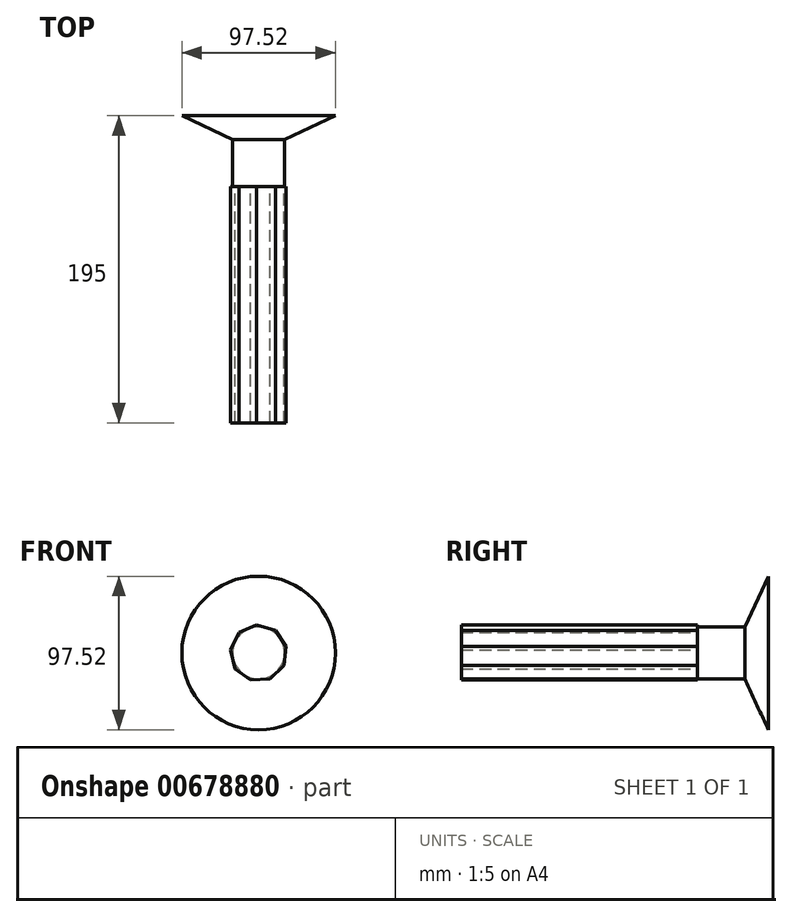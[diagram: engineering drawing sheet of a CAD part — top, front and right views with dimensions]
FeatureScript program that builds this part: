
annotation { "Feature Type Name" : "Feature", "Feature Type Description" : "" }
export const myFeature = defineFeature(function(context is Context, id is Id, definition is map)
    precondition{}
    {
        {
            var Q0;
            Q0=qCreatedBy(makeId("Front.planeOp"),FACE);
            var sketch = newSketch(context, id + "F0", { "sketchPlane" : qUnion([Q0])});
            skLineSegment(sketch, "E0.0", {"start": v(7.22, -16.4) * mm, "end": v(-5.01, -17.2) * mm});
            skLineSegment(sketch, "E0.1", {"start": v(-5.01, -17.2) * mm, "end": v(-14.9, -9.95) * mm});
            skLineSegment(sketch, "E0.2", {"start": v(-14.9, -9.95) * mm, "end": v(-17.8, 1.95) * mm});
            skLineSegment(sketch, "E0.3", {"start": v(-17.8, 1.95) * mm, "end": v(-12.39, 12.94) * mm});
            skLineSegment(sketch, "E0.4", {"start": v(-12.39, 12.94) * mm, "end": v(-1.17, 17.88) * mm});
            skLineSegment(sketch, "E0.5", {"start": v(-1.17, 17.88) * mm, "end": v(10.6, 14.45) * mm});
            skLineSegment(sketch, "E0.6", {"start": v(10.6, 14.45) * mm, "end": v(17.4, 4.26) * mm});
            skLineSegment(sketch, "E0.7", {"start": v(17.4, 4.26) * mm, "end": v(16.07, -7.92) * mm});
            skLineSegment(sketch, "E0.8", {"start": v(16.07, -7.92) * mm, "end": v(7.22, -16.4) * mm});
            skSolve(sketch);
        }
        {
            var Q0;
            Q0=makeQuery(id+"F0.imprint","IMPRINT",FACE,{"disambiguationData":[TD([[makeQuery(id+"F0.imprint","IMPRINT",EDGE,{"derivedFrom":sQuery(id+"F0.wireOp",EDGE,"E0.0")}),-1.0]])]});
            extrude(context, id + "F1", {"entities" : qUnion([Q0]), "depth" : 150 * mm, "offsetDistance" : 25 * mm});
        }
        {
            var Q0;
            Q0=qCreatedBy(makeId("Front.planeOp"),FACE);
            var sketch = newSketch(context, id + "F2", { "sketchPlane" : qUnion([Q0])});
            skCircle(sketch, "E1", {"center": v(0, 0) * mm, "radius": 16.6 * mm});
            skSolve(sketch);
        }
        {
            var Q0;
            Q0=makeQuery(id+"F2.imprint","IMPRINT",FACE,{"disambiguationData":[TD([[makeQuery(id+"F2.imprint","IMPRINT",EDGE,{"derivedFrom":sQuery(id+"F2.wireOp",EDGE,"E1")}),1.0]])]});
            extrude(context, id + "F3", {"entities" : qUnion([Q0]), "operationType" : NewBodyOperationType.ADD, "oppositeDirection" : true, "depth" : 30 * mm, "offsetDistance" : 25 * mm});
        }
        {
            var Q0;
            Q0=makeQuery(id+"F3.opExtrude","CAP_FACE",FACE,{"disambiguationData":[OSD([sQuery(id+"F2.wireOp",EDGE,"E1")])],"isStart":false});
            extrude(context, id + "F4", {"entities" : qUnion([Q0]), "operationType" : NewBodyOperationType.ADD, "depth" : 15 * mm, "offsetDistance" : 25 * mm, "hasDraft" : true, "draftAngle" : 65 * degree});
        }
    });
